# Revit family: Heavy_Duty_Plastic_Lockers-Salsbury_Industries-18_41000_Series-1_Wide_Units
name_source: partatom
category: Specialty Equipment
revit_build: Autodesk Revit 2016 (Build: 20150714_1515(x64)
units: mm (PartAtom-declared; Revit-internal decimal feet)

## family parameters
Always vertical = Yes
Cut with Voids When Loaded = No
OmniClass Number = 23.40.00.00
OmniClass Title = Equipment and Furnishings
Part Type = Normal
Room Calculation Point = No
Round Connector Dimension = Use Diameter
Shared = No
Work Plane-Based = No

## types (2) — shared parameters
Assembly Code = C1030310
Back Enclosure Material = High-density Polyethylene (HDPE) - Salsbury Finish - White
Base Material = High-density Polyethylene (HDPE) - Salsbury Finish - Black
Depth = 18 "
Door Location D1 = Heavy Duty Plastic Locker 18-inch Doors : Single Tier Door
Height = 72 "
Lock Latch Material = Stainless Steel - Salsbury Finish - Polished
Manufacturer = Salsbury Industries
MasterFormat Code = 10 51 26
MasterFormat Title = Plastic Lockers
Mounting Hardware Material = Aluminum - Salsbury Finish - Flat
OmniClass 23 Number = 23.40.00.00
OmniClass 23 Title = Equipment and Furnishings
Type Comments = 18" Wide Heavy Duty Plastic Locker - Single Tier
URL = www.lockers.com
Version = 1.0 (01/30/19)
Visible = Yes
Width = 18 "

## per-type parameters (varying)
| type | Base | Base Height | Description |
| 18-41168 | Heavy Duty Plastic Locker Base : 1 Wide 18" Wide Base | 3 " | 1 Wide - 6 feet high - 18"Deep - with Base |
| 18-41168 - without Base | Heavy Duty Plastic Locker Base : None | 0 " | 1 Wide - 6 feet high - 18"Deep - without Base |

note: column(s) folded — value = type name in every type: Model

## geometry (parser evidence)
native form markers: Sweep x32
no freeform markers — native parametric forms only
